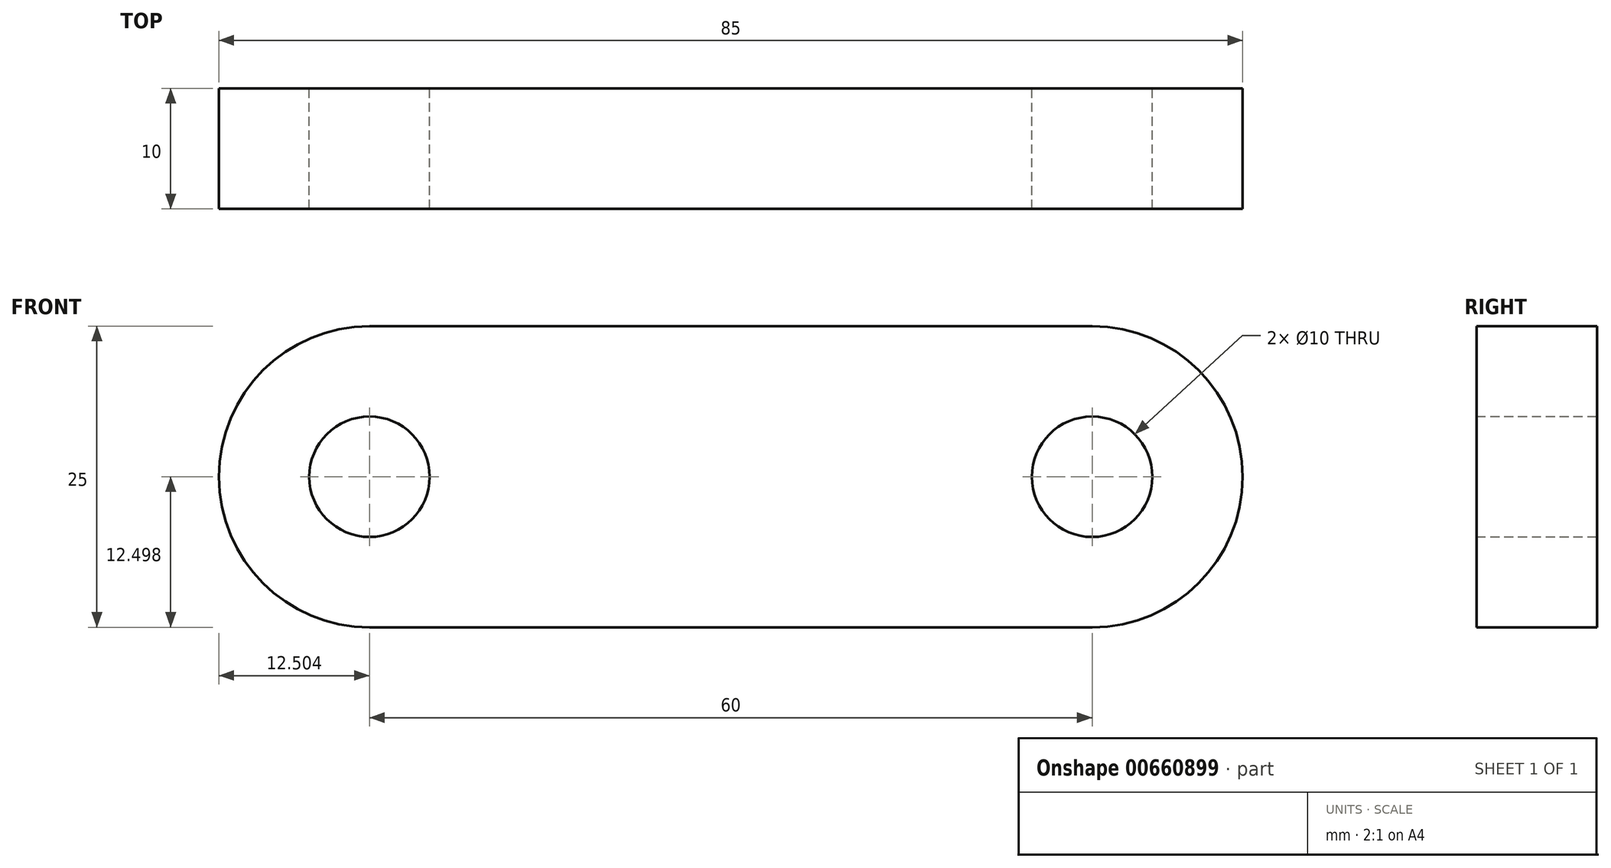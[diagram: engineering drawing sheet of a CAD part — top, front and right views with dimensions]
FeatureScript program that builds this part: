
annotation { "Feature Type Name" : "Feature", "Feature Type Description" : "" }
export const myFeature = defineFeature(function(context is Context, id is Id, definition is map)
    precondition{}
    {
        {
            var Q0;
            Q0=qCreatedBy(makeId("Front.planeOp"),FACE);
            var sketch = newSketch(context, id + "F0", { "sketchPlane" : qUnion([Q0])});
            skLineSegment(sketch, "E0.bottom", {"start": v(-25.07, 15.84) * mm, "end": v(34.93, 15.84) * mm});
            skLineSegment(sketch, "E0.top", {"start": v(-25.07, -9.16) * mm, "end": v(34.93, -9.16) * mm});
            skArc(sketch, "E1", {"start": v(-25.07, 15.84) * mm, "mid": v(-37.57, 3.34) * mm, "end": v(-25.07, -9.16) * mm});
            skArc(sketch, "E2", {"start": v(34.93, -9.16) * mm, "mid": v(47.43, 3.34) * mm, "end": v(34.93, 15.84) * mm});
            skCircle(sketch, "E3", {"center": v(-25.07, 3.34) * mm, "radius": 5 * mm});
            skCircle(sketch, "E4", {"center": v(34.93, 3.34) * mm, "radius": 5 * mm});
            skSolve(sketch);
        }
        {
            var Q0;
            Q0 = qSketchRegion(id + "F0", true);
            extrude(context, id + "F1", {"entities" : qUnion([Q0]), "depth" : 10 * mm, "offsetDistance" : 25.4 * mm});
        }
    });
